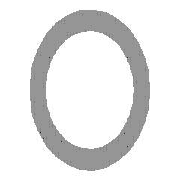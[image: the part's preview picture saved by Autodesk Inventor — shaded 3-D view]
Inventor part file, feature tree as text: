
AUTODESK INVENTOR PART (.ipt)
format: ipt  version: 2021 (Build 250183000, 183)  size: 754,688 bytes
history: native  units: mm (DEFAULTED — no unit token found)
features: other x15, plane x4, sketch x4, split x2, sweep x1
ambient origin geometry x8: Origin, YZ Plane, XZ Plane, XY Plane, X Axis, Y Axis, Z Axis, Center Point
bodies: Solid1 (feature_tree)
feature tree (26):
  parser-record x1  (decoder bookkeeping rows leaked as tree rows — omitted from the tree; the rows remain in map.json)
  other  "Driven Length"
  other  "Plano inicial"
  other  "Plano final"
  other  "Trayectoria de barrido"
  plane  "Plano de trabajo de orientación"
  sweep  "Cuerpo"
  plane  "Plano de trabajo5"
  split  "Dividir1"
  plane  "Plano de trabajo6"
  split  "Dividir2"
  sketch  "Sketch3"  dims[d0=26.67mm d1=2.8702mm]
  plane  "Work Plane3"
  sketch  "Sketch4"  dims[d4=-0.0mm]
  sketch  "Boceto5"  dims[d5=1146.328138mm]
  other  "Sup1"
  sketch  "Boceto6"  dims[d6=90.0deg d7=1146.328138mm d8=0.0mm d9=0.0mm d10=0.0mm d11=90.0deg d12=0.0mm d13=90.0deg d22=16.002mm d23=53.080004mm d24=0.0mm d25=90.0deg d26=0.0mm d27=90.0deg d32=5.0mm d33=0.0mm d34=5.0mm d35=0.0mm]
  other  "Sup8"
  other  "Sup13"
  other  "Sup14"
  other  "Sólido5"
  other  "SuperficieSolevación1"
  other  "SuperficieSolevación2"
  other  "Sup12"
  other  "Superficie de contorno7"
  other  "Superficie de contorno8"
